# Revit family: Faucet-Lavatory-KOHLER-Avid-K-97347BR_1
name_source: partatom
category: Plumbing Fixtures
revit_build: Autodesk Revit 2017 (Build: 20160225_1515(x64)
units: mm (PartAtom-declared; Revit-internal decimal feet)

## family parameters
Cut with Voids When Loaded = No
Host = Face
OmniClass Number = 23.31.11.00
Part Type = Normal
Room Calculation Point = No
Round Connector Dimension = Use Diameter
Shared = No

## types (3) — shared parameters
ADA Compliant = No
Assembly Code = D2010
CW Connection = Yes
Cold Water Inlet = Cold Water Inlet
Date Modified = 09/24/2020
Default Elevation = 36"
Description = High spout mixer tap for washbasin
Drain Included = No
Flow Rate = 2 GPM
HW Connection = Yes
Handle Clearance = 6 1/2"
Height = 9 15/16"
Hot Water Inlet = Hot Water Inlet
Length = 5 13/16"
Manufacturer = KOHLER Co.
Master Format 2014 = 22 41 39
Master Format 2014 Name = Residential Faucets, Supplies, and Trim
Material = Brass Construction
Pressure = 80.00 psi
Product Name = Avid
Product Page URL = https://br.kohler.com
Spout Reach = 5 13/16"
URL = https://br.kohler.com
Vent Connection = No
Waste Connection = No
Waste Water Outlet = Waste Water Outlet
WaterSense Certified = No
Width = 2"

## per-type parameters (varying)
| type | Finish | Model | Type |
| CP-Polished Chrome | Kohler-Metal-CP-Polished_Chrome | K-97347BR-4ND-CP | 1 |
| TT-Titanium | Kohler-Metal-TT-Vibrant_Titanium | K-97347BR-4ND-TT | 2 |
| BN-Brushed Nickel | Kohler-Metal-BN-Vibrant_Brushed_Nickel | K-97347BR-4ND-BN | 3 |

## geometry (parser evidence)
native form markers: Sweep x4
no freeform markers — native parametric forms only
